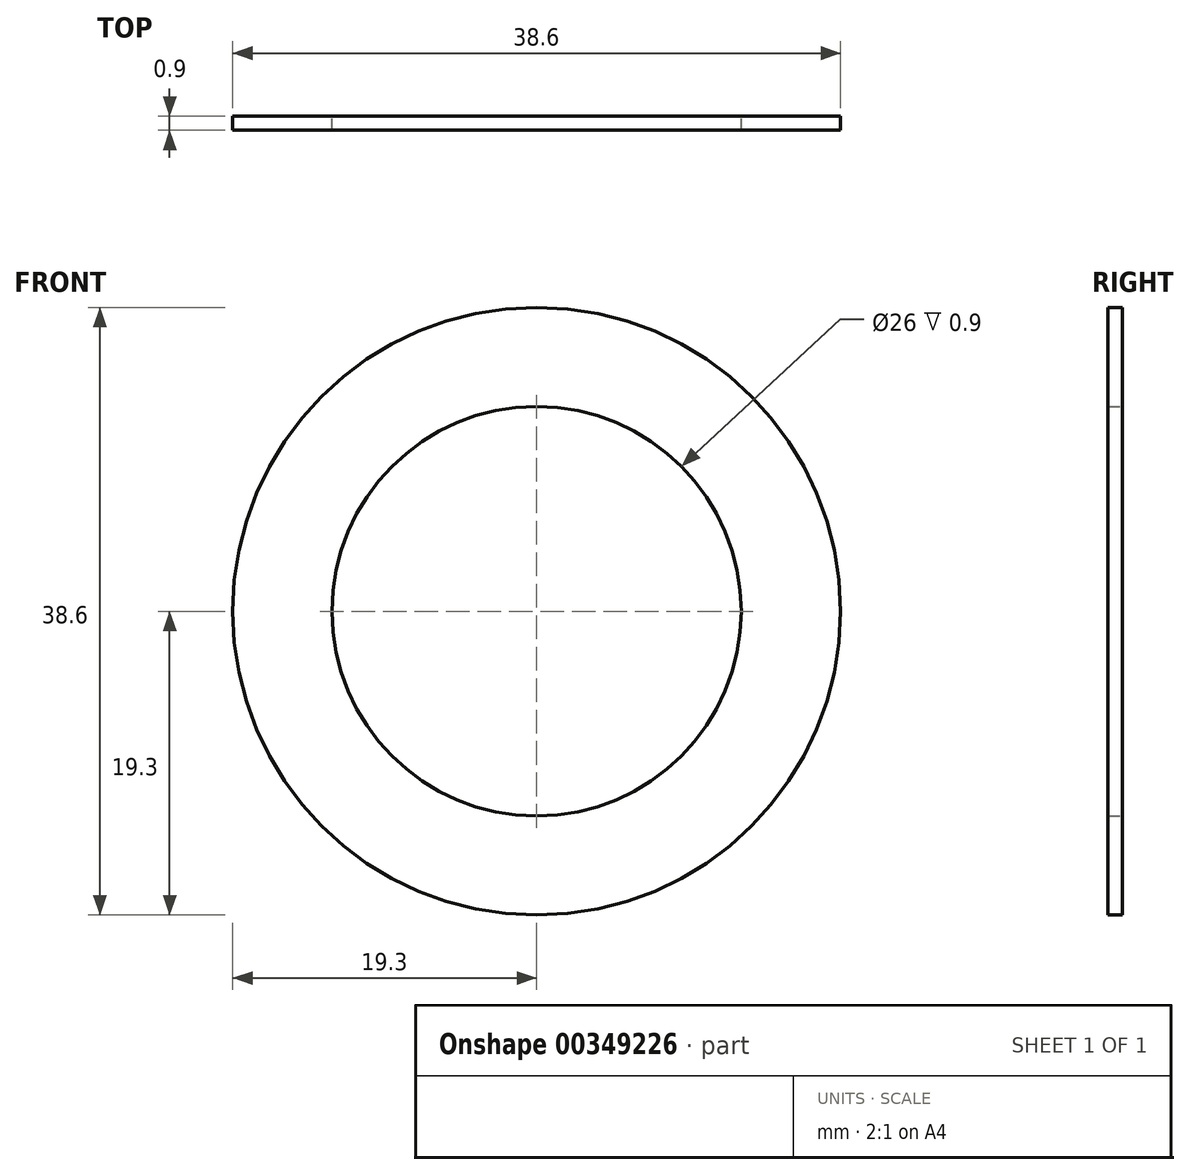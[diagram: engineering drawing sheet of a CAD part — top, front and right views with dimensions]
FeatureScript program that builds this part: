
annotation { "Feature Type Name" : "Feature", "Feature Type Description" : "" }
export const myFeature = defineFeature(function(context is Context, id is Id, definition is map)
    precondition{}
    {
        {
            var Q0;
            Q0=qCreatedBy(makeId("Front.planeOp"),FACE);
            var sketch = newSketch(context, id + "F0", { "sketchPlane" : qUnion([Q0])});
            skCircle(sketch, "E0", {"center": v(0, 0) * mm, "radius": 19.3 * mm});
            skCircle(sketch, "E1", {"center": v(0, 0) * mm, "radius": 13 * mm});
            skSolve(sketch);
        }
        {
            var Q0;
            Q0=makeQuery(id+"F0.imprint","IMPRINT",FACE,{"disambiguationData":[TD([[makeQuery(id+"F0.imprint","IMPRINT",EDGE,{"derivedFrom":sQuery(id+"F0.wireOp",EDGE,"E0")}),1.0]])]});
            extrude(context, id + "F1", {"entities" : qUnion([Q0]), "depth" : 0.9 * mm});
        }
    });
